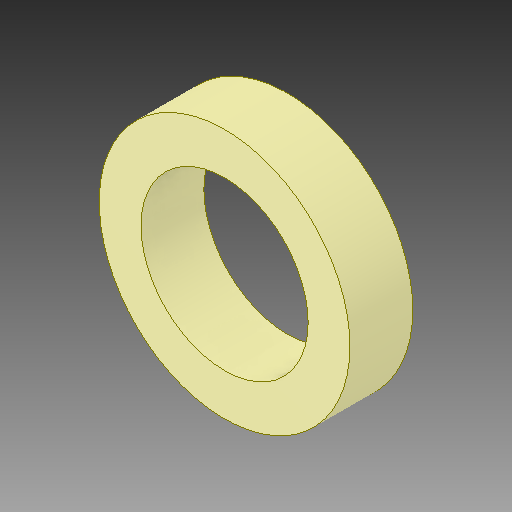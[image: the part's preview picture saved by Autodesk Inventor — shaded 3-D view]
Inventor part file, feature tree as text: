
AUTODESK INVENTOR PART (.ipt)
format: ipt  version: 2019 (Build 230136000, 136)  size: 97,280 bytes
history: native  units: in
note: dims shown in document units (in); Inventor stores cm internally (conversion verified against a paired STEP export)
features: revolve x1
ambient origin geometry x8: Origin, YZ Plane, XZ Plane, XY Plane, X Axis, Y Axis, Z Axis, Center Point
bodies: Solid1 (feature_tree)
feature tree (1):
  revolve  "Revolve1"  [1 undecoded]
note: 1 required parameter value undecoded (feature->parameter linkage not recoverable at this tier; creation-order binding heuristic only, values carry confidence <= 0.55)
